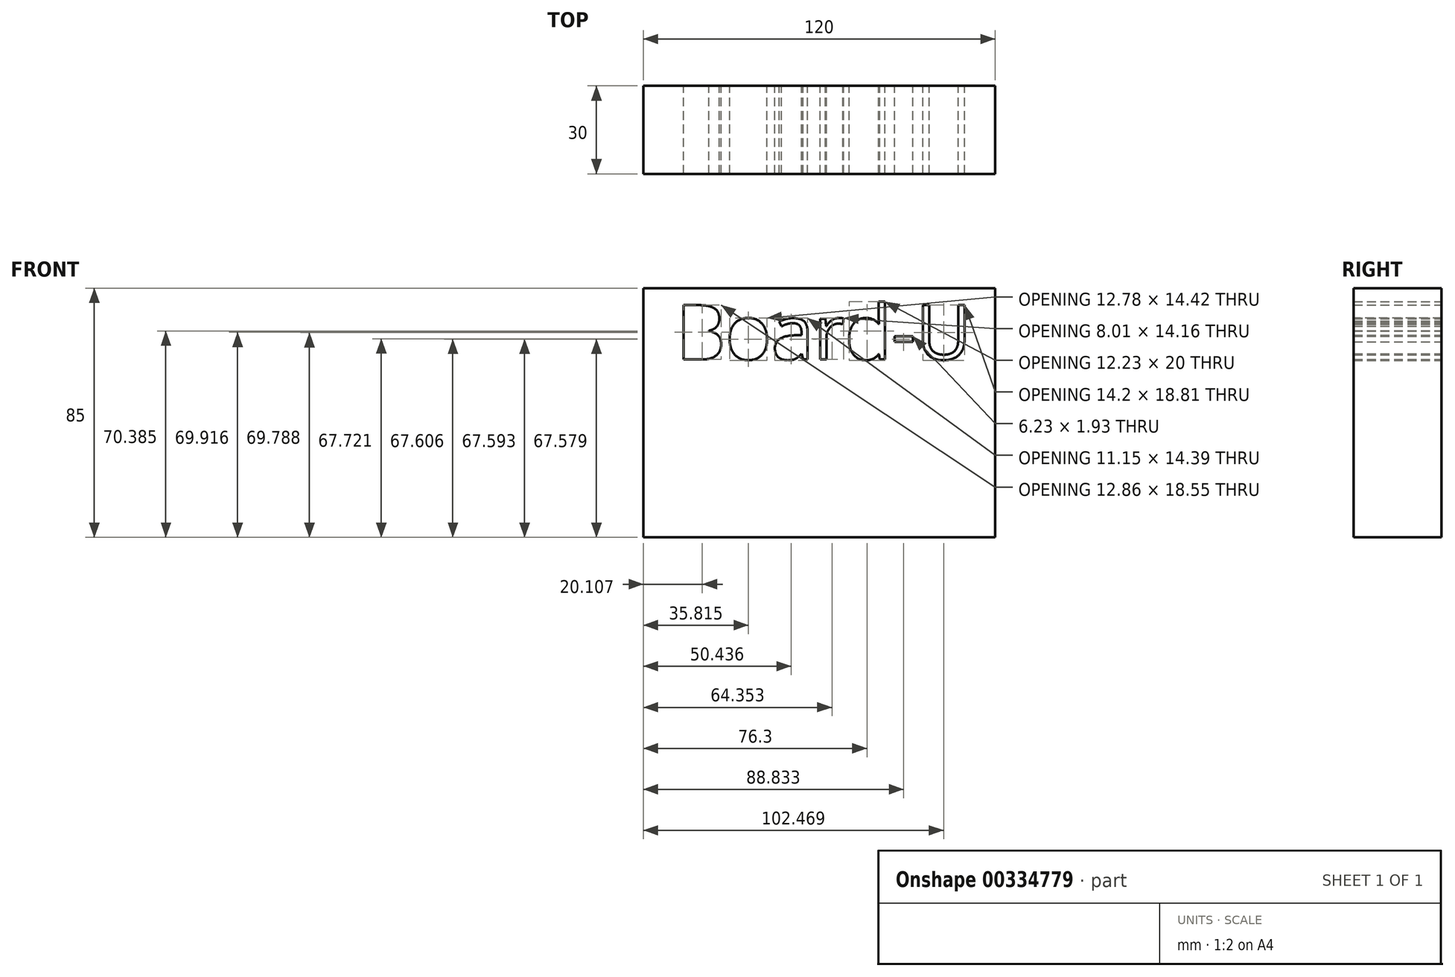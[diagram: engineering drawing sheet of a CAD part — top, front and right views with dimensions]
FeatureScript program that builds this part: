
annotation { "Feature Type Name" : "Feature", "Feature Type Description" : "" }
export const myFeature = defineFeature(function(context is Context, id is Id, definition is map)
    precondition{}
    {
        {
            var Q0;
            Q0=qCreatedBy(makeId("Front.planeOp"),FACE);
            var sketch = newSketch(context, id + "F0", { "sketchPlane" : qUnion([Q0])});
            skLineSegment(sketch, "E0.bottom", {"start": v(-14.99, 0) * mm, "end": v(-134.99, 0) * mm});
            skLineSegment(sketch, "E0.top", {"start": v(-14.99, -85) * mm, "end": v(-134.99, -85) * mm});
            skLineSegment(sketch, "E0.left", {"start": v(-14.99, 0) * mm, "end": v(-14.99, -85) * mm});
            skLineSegment(sketch, "E0.right", {"start": v(-134.99, 0) * mm, "end": v(-134.99, -85) * mm});
            skText(sketch, "E1", { "text": "Board-U", "fontName": "OpenSans-Regular.ttf"});
            const initialGuessF0  = {"E1": [-0.12386, -0.02436, 1, 0, 0.01871]};
            skSetInitialGuess(sketch, initialGuessF0);
            skSolve(sketch);
        }
        {
            var Q0;
            Q0=makeQuery(id+"F0.imprint","IMPRINT",FACE,{"disambiguationData":[TD([[makeQuery(id+"F0.imprint","IMPRINT",EDGE,{"derivedFrom":sQuery(id+"F0.wireOp",EDGE,"E0.bottom")}),1.0]])]});
            extrude(context, id + "F1", {"entities" : qUnion([Q0]), "depth" : 30 * mm});
        }
    });
